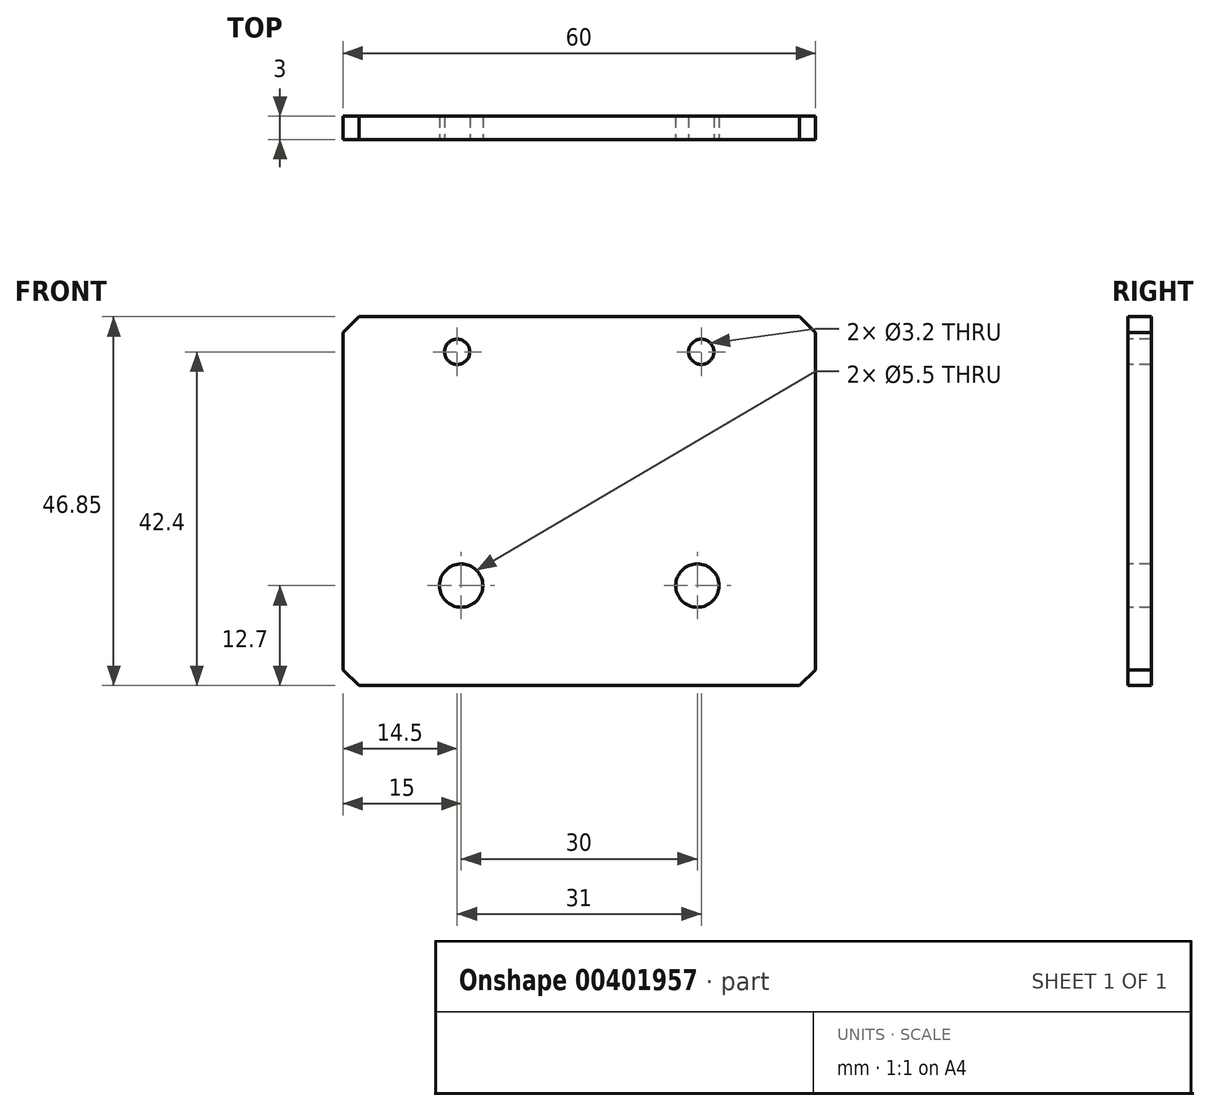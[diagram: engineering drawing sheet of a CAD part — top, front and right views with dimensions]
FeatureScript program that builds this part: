
annotation { "Feature Type Name" : "Feature", "Feature Type Description" : "" }
export const myFeature = defineFeature(function(context is Context, id is Id, definition is map)
    precondition{}
    {
        {
            var Q0;
            Q0=qCreatedBy(makeId("Front.planeOp"),FACE);
            var sketch = newSketch(context, id + "F0", { "sketchPlane" : qUnion([Q0])});
            skLineSegment(sketch, "E0.bottom", {"start": v(0, 0) * mm, "end": v(60, 0) * mm});
            skLineSegment(sketch, "E0.top", {"start": v(0, 46.85) * mm, "end": v(60, 46.85) * mm});
            skLineSegment(sketch, "E0.left", {"start": v(0, 0) * mm, "end": v(0, 46.85) * mm});
            skLineSegment(sketch, "E0.right", {"start": v(60, 0) * mm, "end": v(60, 46.85) * mm});
            skLineSegment(sketch, "E1", {"start": v(0, 25.4) * mm, "end": v(60, 25.4) * mm, "construction": true});
            skCircle(sketch, "E2", {"center": v(15, 12.7) * mm, "radius": 2.75 * mm});
            skCircle(sketch, "E3", {"center": v(45, 12.7) * mm, "radius": 2.75 * mm});
            skLineSegment(sketch, "E4", {"start": v(30, 25.4) * mm, "end": v(30, 0) * mm, "construction": true});
            skLineSegment(sketch, "E5", {"start": v(30, 12.7) * mm, "end": v(0, 12.7) * mm, "construction": true});
            skLineSegment(sketch, "E6", {"start": v(30, 12.7) * mm, "end": v(60, 12.7) * mm, "construction": true});
            skCircle(sketch, "E7", {"center": v(14.5, 42.4) * mm, "radius": 1.6 * mm});
            skCircle(sketch, "E8", {"center": v(45.5, 42.4) * mm, "radius": 1.6 * mm});
            skLineSegment(sketch, "E9", {"start": v(14.5, 42.4) * mm, "end": v(45.5, 42.4) * mm, "construction": true});
            skLineSegment(sketch, "E10", {"start": v(30, 42.4) * mm, "end": v(30, 46.85) * mm, "construction": true});
            skLineSegment(sketch, "E11", {"start": v(0, 115.8) * mm, "end": v(60, 115.8) * mm, "construction": true});
            skLineSegment(sketch, "E12", {"start": v(30, 115.8) * mm, "end": v(30, 0) * mm, "construction": true});
            skLineSegment(sketch, "E13", {"start": v(30, 57.9) * mm, "end": v(90.54, 57.9) * mm, "construction": true});
            skSolve(sketch);
        }
        {
            var Q0;
            Q0 = qSketchRegion(id + "F0", true);
            extrude(context, id + "F1", {"entities" : qUnion([Q0]), "oppositeDirection" : true, "depth" : 3 * mm});
        }
        {
            var Q0;
            Q0=makeQuery(id+"F1.opExtrude","SWEPT_EDGE",EDGE,{"disambiguationData":[OSD([sQuery(id+"F0.wireOp",EDGE,"E0.top"),sQuery(id+"F0.wireOp",EDGE,"E0.left")])]});
            var Q1;
            Q1=makeQuery(id+"F1.opExtrude","SWEPT_EDGE",EDGE,{"disambiguationData":[OSD([sQuery(id+"F0.wireOp",EDGE,"E0.bottom"),sQuery(id+"F0.wireOp",EDGE,"E0.left")])]});
            var Q2;
            Q2=makeQuery(id+"F1.opExtrude","SWEPT_EDGE",EDGE,{"disambiguationData":[OSD([sQuery(id+"F0.wireOp",EDGE,"E0.bottom"),sQuery(id+"F0.wireOp",EDGE,"E0.right")])]});
            var Q3;
            Q3=makeQuery(id+"F1.opExtrude","SWEPT_EDGE",EDGE,{"disambiguationData":[OSD([sQuery(id+"F0.wireOp",EDGE,"E0.top"),sQuery(id+"F0.wireOp",EDGE,"E0.right")])]});
            chamfer(context, id + "F2", {"entities" : qUnion([Q0, Q1, Q2, Q3]), "width" : 2 * mm, "tangentPropagation" : true});
        }
    });
